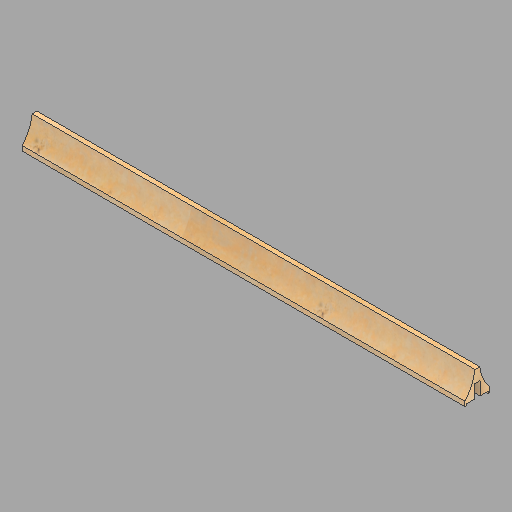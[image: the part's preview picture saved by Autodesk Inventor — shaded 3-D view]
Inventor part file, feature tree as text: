
AUTODESK INVENTOR PART (.ipt)
format: ipt  version: 2022.2 (Build 262287010, 287A)  size: 178,688 bytes
history: native  units: in
note: dims shown in document units (in); Inventor stores cm internally (conversion verified against a paired STEP export)
features: revolve x2, other x1, direct_edit x1
ambient origin geometry x8: Origin, YZ Plane, XZ Plane, XY Plane, X Axis, Y Axis, Z Axis, Center Point
bodies: Solid1 (feature_tree)
feature tree (4):
  other  "Mull (Lower)"
  direct_edit  "Direct Edit1"
  revolve  "Rotate1"  [1 undecoded]
  revolve  "Rotate2"  Angle=180.0deg
note: 1 required parameter value undecoded (feature->parameter linkage not recoverable at this tier; creation-order binding heuristic only, values carry confidence <= 0.55)
